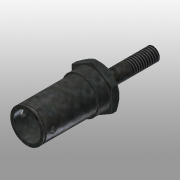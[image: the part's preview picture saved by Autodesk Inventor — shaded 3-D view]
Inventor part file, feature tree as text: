
AUTODESK INVENTOR PART (.ipt)
format: ipt  version: 2016 (Build 200138000, 138)  size: 178,688 bytes
history: native  units: mm
features: sketch x8, extrude x6, revolve x2, thread x1, projected_geometry x1
ambient origin geometry x8: Origin, YZ Plane, XZ Plane, XY Plane, X Axis, Y Axis, Z Axis, Center Point
bodies: Solid1 (feature_tree)
feature tree (18):
  extrude  "Extrusion1"  Depth=2.5mm TaperAngle=0.0deg
  extrude  "Extrusion2"  Depth=15.8mm TaperAngle=0.0deg
  thread  "Thread1"  [1 undecoded]
  extrude  "Extrusion3"  Depth=3.44mm TaperAngle=0.0deg
  extrude  "Extrusion4"  Depth=10.0mm TaperAngle=0.0deg
  extrude  "Extrusion5"  Depth=10.0mm TaperAngle=0.0deg
  extrude  "Extrusion6"  Depth=3.0mm
  revolve  "Revolution1"  [1 undecoded]
  revolve  "Revolution2"  Angle=90.0deg
  sketch  "Sketch1"  dims[d0=12.0mm d1=2.5mm d2=0.0mm]
  sketch  "Sketch2"  dims[d3=4.0mm d4=15.8mm d5=0.0mm d6=8.0mm d7=0.0mm]
  sketch  "Sketch3"  dims[d8=11.0mm d9=3.44mm d10=0.0mm]
  sketch  "Sketch4"  dims[d11=10.0mm d12=16.0mm d13=0.0mm]
  sketch  "Sketch5"  dims[d14=8.0mm d15=10.0mm d16=0.0mm]
  sketch  "Sketch6"  dims[d17=2.0mm d18=3.0mm]
  sketch  "Sketch7"  dims[d19=14.0mm d20=0.0mm d21=0.6mm]
  sketch  "Sketch8"  dims[d22=0.6mm d23=90.0deg d24=45.0deg d25=90.0deg]
  projected_geometry  "Project Cut Edges1"
note: 2 required parameter values undecoded (feature->parameter linkage not recoverable at this tier; creation-order binding heuristic only, values carry confidence <= 0.55)